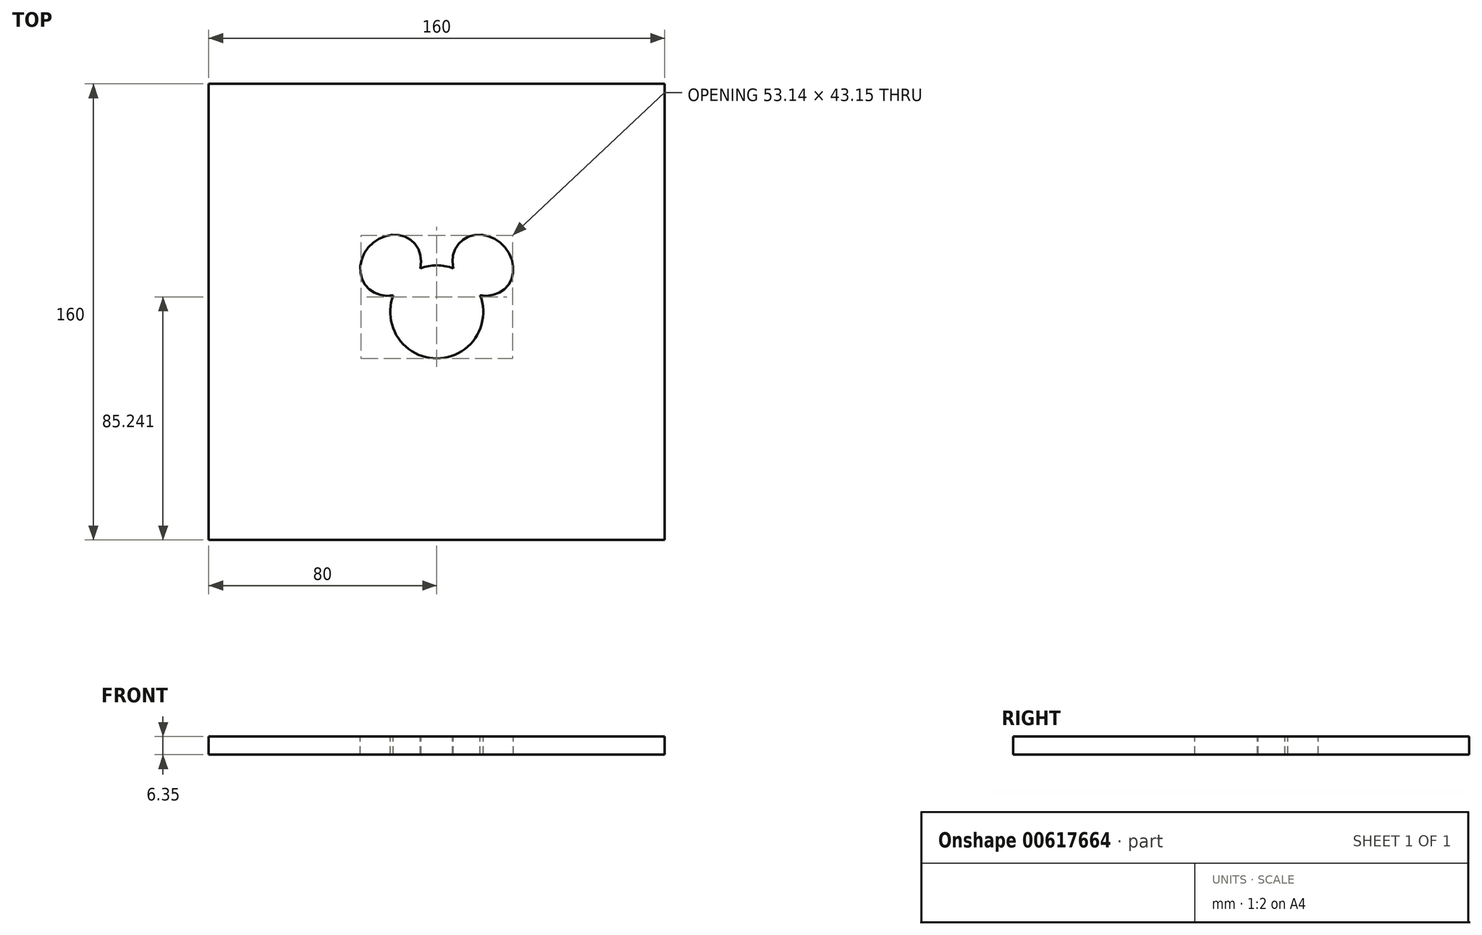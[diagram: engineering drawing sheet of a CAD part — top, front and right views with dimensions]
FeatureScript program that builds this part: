
annotation { "Feature Type Name" : "Feature", "Feature Type Description" : "" }
export const myFeature = defineFeature(function(context is Context, id is Id, definition is map)
    precondition{}
    {
        {
            var Q0;
            Q0=qCreatedBy(makeId("Top.planeOp"),FACE);
            var sketch = newSketch(context, id + "F0", { "sketchPlane" : qUnion([Q0])});
            skLineSegment(sketch, "E0.bottom", {"start": v(80, -80) * mm, "end": v(-80, -80) * mm});
            skLineSegment(sketch, "E0.top", {"start": v(80, 80) * mm, "end": v(-80, 80) * mm});
            skLineSegment(sketch, "E0.left", {"start": v(80, -80) * mm, "end": v(80, 80) * mm});
            skLineSegment(sketch, "E0.right", {"start": v(-80, -80) * mm, "end": v(-80, 80) * mm});
            skPoint(sketch, "E0.middle", {"position": v(0, 0) * mm});
            skSolve(sketch);
        }
        {
            var Q0;
            Q0=makeQuery(id+"F0.imprint","IMPRINT",FACE,{"disambiguationData":[TD([[makeQuery(id+"F0.imprint","IMPRINT",EDGE,{"derivedFrom":sQuery(id+"F0.wireOp",EDGE,"E0.bottom")}),-1.0]])]});
            var sketch = newSketch(context, id + "F1", { "sketchPlane" : qUnion([Q0])});
            skCircle(sketch, "E1", {"center": v(0, 0) * mm, "radius": 16.34 * mm});
            skEllipse(sketch, "E2.MirrorC", {"center": v(-16.16, 16.36) * mm, "majorRadius": 11.34 * mm, "minorRadius": 10 * mm, "majorAxis": v(0.7, 0.71)});
            skEllipse(sketch, "E3.MirrorC", {"center": v(16.16, 16.36) * mm, "majorRadius": 11.34 * mm, "minorRadius": 10 * mm, "majorAxis": v(-0.7, 0.71)});
            skSolve(sketch);
        }
        {
            var Q0;
            Q0=makeQuery(id+"F0.imprint","IMPRINT",FACE,{"disambiguationData":[TD([[makeQuery(id+"F0.imprint","IMPRINT",EDGE,{"derivedFrom":sQuery(id+"F0.wireOp",EDGE,"E0.bottom")}),-1.0]])]});
            extrude(context, id + "F2", {"entities" : qUnion([Q0]), "oppositeDirection" : true, "depth" : 6.35 * mm, "offsetDistance" : 25 * mm});
        }
        {
            var Q0;
            {var subQ0=sQuery(id+"F1.wireOp",EDGE,"E2.MirrorC");var subQ1=sQuery(id+"F1.wireOp",EDGE,"E1");var subQ2=makeQuery(id+"F1.imprint","INTERSECT",VERTEX,{"disambiguationData":[OD(0.0)],"derivedFrom":[subQ1,subQ0]});Q0=makeQuery(id+"F1.imprint","IMPRINT",FACE,{"disambiguationData":[TD([[makeQuery(id+"F1.imprint","IMPRINT",EDGE,{"disambiguationData":[TD([[subQ2,-1.0]])],"derivedFrom":subQ1}),-1.0]])]});}
            extrude(context, id + "F3", {"entities" : qUnion([Q0]), "operationType" : NewBodyOperationType.REMOVE, "endBound" : BoundingType.THROUGH_ALL, "oppositeDirection" : true, "depth" : 25 * mm, "offsetDistance" : 25 * mm});
        }
        {
            var Q0;
            {var subQ0=sQuery(id+"F1.wireOp",EDGE,"E3.MirrorC");var subQ1=sQuery(id+"F1.wireOp",EDGE,"E1");var subQ2=makeQuery(id+"F1.imprint","INTERSECT",VERTEX,{"disambiguationData":[OD(0.0)],"derivedFrom":[subQ1,subQ0]});Q0=makeQuery(id+"F1.imprint","IMPRINT",FACE,{"disambiguationData":[TD([[makeQuery(id+"F1.imprint","IMPRINT",EDGE,{"disambiguationData":[TD([[subQ2,-1.0]])],"derivedFrom":subQ1}),1.0]])]});}
            extrude(context, id + "F4", {"entities" : qUnion([Q0]), "operationType" : NewBodyOperationType.REMOVE, "oppositeDirection" : true, "depth" : 25 * mm, "offsetDistance" : 25 * mm});
        }
        {
            var Q0;
            {var subQ0=sQuery(id+"F1.wireOp",EDGE,"E3.MirrorC");var subQ1=sQuery(id+"F1.wireOp",EDGE,"E1");var subQ2=makeQuery(id+"F1.imprint","INTERSECT",VERTEX,{"disambiguationData":[OD(0.0)],"derivedFrom":[subQ1,subQ0]});Q0=makeQuery(id+"F1.imprint","IMPRINT",FACE,{"disambiguationData":[TD([[makeQuery(id+"F1.imprint","IMPRINT",EDGE,{"disambiguationData":[TD([[subQ2,1.0]])],"derivedFrom":subQ1}),-1.0]])]});}
            extrude(context, id + "F5", {"entities" : qUnion([Q0]), "operationType" : NewBodyOperationType.REMOVE, "oppositeDirection" : true, "depth" : 25 * mm, "offsetDistance" : 25 * mm});
        }
        {
            var Q0;
            {var subQ0=sQuery(id+"F1.wireOp",EDGE,"E2.MirrorC");var subQ1=sQuery(id+"F1.wireOp",EDGE,"E1");var subQ2=makeQuery(id+"F1.imprint","INTERSECT",VERTEX,{"disambiguationData":[OD(0.0)],"derivedFrom":[subQ1,subQ0]});Q0=makeQuery(id+"F1.imprint","IMPRINT",FACE,{"disambiguationData":[TD([[makeQuery(id+"F1.imprint","IMPRINT",EDGE,{"disambiguationData":[TD([[subQ2,-1.0]])],"derivedFrom":subQ1}),1.0]])]});}
            extrude(context, id + "F6", {"entities" : qUnion([Q0]), "operationType" : NewBodyOperationType.REMOVE, "oppositeDirection" : true, "depth" : 25 * mm, "offsetDistance" : 25 * mm});
        }
        {
            var Q0;
            {var subQ0=sQuery(id+"F1.wireOp",EDGE,"E3.MirrorC");var subQ1=sQuery(id+"F1.wireOp",EDGE,"E1");var subQ2=makeQuery(id+"F1.imprint","INTERSECT",VERTEX,{"disambiguationData":[OD(0.0)],"derivedFrom":[subQ1,subQ0]});Q0=makeQuery(id+"F1.imprint","IMPRINT",FACE,{"disambiguationData":[TD([[makeQuery(id+"F1.imprint","IMPRINT",EDGE,{"disambiguationData":[TD([[subQ2,1.0]])],"derivedFrom":subQ1}),1.0]])]});}
            extrude(context, id + "F7", {"entities" : qUnion([Q0]), "operationType" : NewBodyOperationType.REMOVE, "oppositeDirection" : true, "depth" : 25 * mm, "offsetDistance" : 25 * mm});
        }
    });
